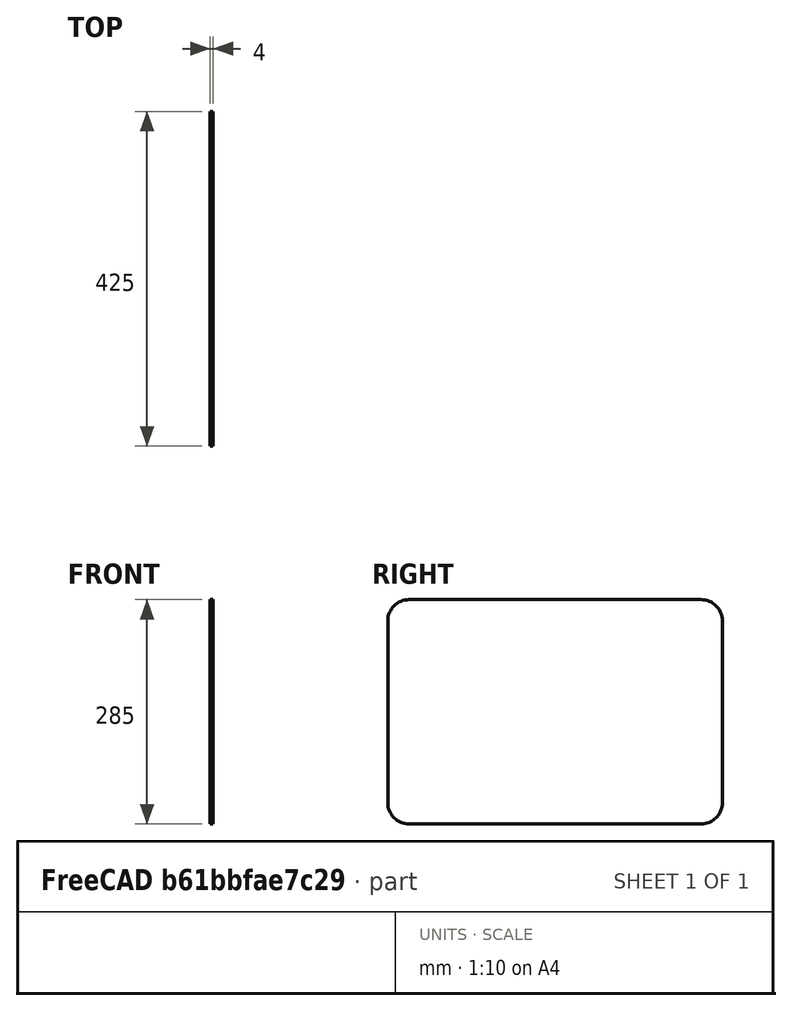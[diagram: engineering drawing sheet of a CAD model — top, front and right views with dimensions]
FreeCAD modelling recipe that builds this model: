
FCSTD DOCUMENT  (FreeCAD 0.20R29603 (Git))
Label: Scheibe_440x300
License: All rights reserved
LicenseURL: http://en.wikipedia.org/wiki/All_rights_reserved
objects: Sketcher::SketchObject×1, PartDesign::Pad×1, PartDesign::Body×1
note: 4 computed .brp shape members not serialized (recipe doc carries the construction recipe); baked Part::Feature solids carry a one-line shape summary decoded from their .brp

FEATURE [Sketcher::SketchObject] Sketch
  FullyConstrained = true
  MapMode = 5
  Placement = pos=(0,0,0) rot=(0.57735,0.57735,0.57735;2.0944rad)
  Support = -> [YZ_Plane]
  sketch-geometry (13):
    g0: LineSegment StartX=-212.5 StartY=115.5 StartZ=0 EndX=-212.5 EndY=-115.5 EndZ=0
    g1: LineSegment StartX=-185.5 StartY=-142.5 StartZ=0 EndX=185.5 EndY=-142.5 EndZ=0
    g2: LineSegment StartX=212.5 StartY=-115.5 StartZ=0 EndX=212.5 EndY=115.5 EndZ=0
    g3: LineSegment StartX=185.5 StartY=142.5 StartZ=0 EndX=-185.5 EndY=142.5 EndZ=0
    g4: GeomPoint X=0 Y=0 Z=0
    g5: ArcOfCircle CenterX=-185.5 CenterY=115.5 CenterZ=0 NormalX=0 NormalY=0 NormalZ=1 AngleXU=0 Radius=27 StartAngle=1.5708 EndAngle=3.14159
    g6: GeomPoint X=-212.5 Y=142.5 Z=0
    g7: ArcOfCircle CenterX=185.5 CenterY=115.5 CenterZ=0 NormalX=0 NormalY=0 NormalZ=1 AngleXU=0 Radius=27 StartAngle=0 EndAngle=1.5708
    g8: GeomPoint X=212.5 Y=142.5 Z=0
    g9: ArcOfCircle CenterX=-185.5 CenterY=-115.5 CenterZ=0 NormalX=0 NormalY=0 NormalZ=1 AngleXU=0 Radius=27 StartAngle=3.14159 EndAngle=4.71239
    g10: GeomPoint X=-212.5 Y=-142.5 Z=0
    g11: ArcOfCircle CenterX=185.5 CenterY=-115.5 CenterZ=0 NormalX=0 NormalY=0 NormalZ=1 AngleXU=0 Radius=27 StartAngle=4.71239 EndAngle=6.28319
    g12: GeomPoint X=212.5 Y=-142.5 Z=0
  constraints (28):
    c: Horizontal(g1)
    c: Horizontal(g3)
    c: Vertical(g0)
    c: Vertical(g2)
    c: Symmetric(g12,g6,g4)
    c: Coincident(g4,g-1)
    c: Distance(g8,g6) = 425
    c: Distance(g10,g6) = 285
    c: PointOnObject(g6,g0)
    c: PointOnObject(g6,g3)
    c: Tangent(g0,g5) = -1.5708
    c: Tangent(g3,g5) = -1.5708
    c: PointOnObject(g8,g2)
    c: PointOnObject(g8,g3)
    c: Tangent(g2,g7) = -1.5708
    c: Tangent(g3,g7) = -1.5708
    c: PointOnObject(g10,g0)
    c: PointOnObject(g10,g1)
    c: Tangent(g0,g9) = -1.5708
    c: Tangent(g1,g9) = -1.5708
    c: PointOnObject(g12,g1)
    c: PointOnObject(g12,g2)
    c: Tangent(g1,g11) = -1.5708
    c: Tangent(g2,g11) = -1.5708
    c: Equal(g5,g7)
    c: Equal(g7,g11)
    c: Equal(g11,g9)
    c: Radius(g7) = 27
FEATURE [PartDesign::Pad] Pad
  Direction = (1,-2e-16,3e-16)
  Length = 4
  Length2 = 10
  Placement = pos=(0,0,0) rot=(0.57735,0.57735,0.57735;2.0944rad)
  Profile = -> Sketch
  ReferenceAxis = -> Sketch [N_Axis]
  Type = 0
FEATURE [PartDesign::Body] Body
  Group = -> [Sketch,Pad]
  Origin = -> Origin
  Tip = -> Pad
